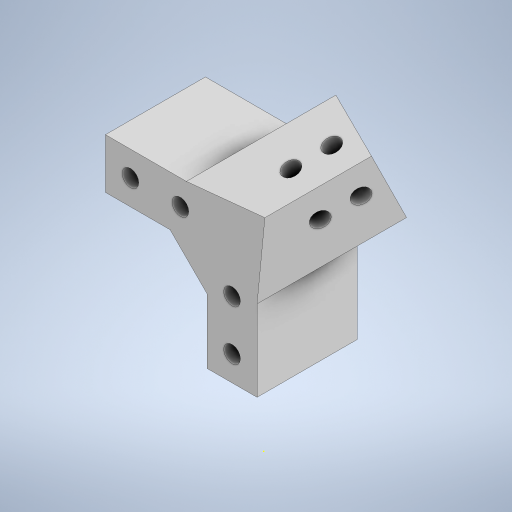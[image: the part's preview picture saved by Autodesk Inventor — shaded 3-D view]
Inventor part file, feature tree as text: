
AUTODESK INVENTOR PART (.ipt)
format: ipt  version: 2024.3 (Build 283343000, 343)  size: 352,768 bytes
history: native  units: mm
features: sketch x11, extrude x7, projected_geometry x5, hole x3, other x1
ambient origin geometry x8: Origin, YZ Plane, XZ Plane, XY Plane, X Axis, Y Axis, Z Axis, Center Point
bodies: Body1 (feature_tree)
feature tree (27):
  other  "ソリッド1"
  extrude  "押し出し1"  Depth=60.0mm
  hole  "穴1"  [1 undecoded]
  extrude  "押し出し2"  Depth=30.0mm TaperAngle=0.0deg
  extrude  "押し出し11"  Depth=7.5mm
  extrude  "押し出し12"  Depth=7.5mm
  extrude  "押し出し17"  Depth=10.5mm
  extrude  "押し出し18"  Depth=10.5mm
  sketch  "スケッチ27"
  extrude  "押し出し19"  Depth=15.0mm
  hole  "穴4"  [1 undecoded]
  hole  "穴5"  [1 undecoded]
  sketch  "スケッチ1"
  sketch  "スケッチ2"
  sketch  "スケッチ3"
  projected_geometry  "投影ループ1"
  sketch  "スケッチ15"
  projected_geometry  "投影ループ10"
  sketch  "スケッチ16"
  projected_geometry  "投影ループ11"
  sketch  "スケッチ25"
  projected_geometry  "投影ループ18"
  sketch  "スケッチ26"
  projected_geometry  "投影ループ19"
  sketch  "スケッチ28"
  sketch  "スケッチ29"
  sketch  "スケッチ30"
note: 3 required parameter values undecoded (feature->parameter linkage not recoverable at this tier; creation-order binding heuristic only, values carry confidence <= 0.55)
